# Revit family: Electronics_Visual-TVs_ViewSonic_The-ViewSonicR-CDE7500-Series-Large-Form
name_source: partatom
category: Electrical Equipment
revit_build: Autodesk Revit 2015 (Build: 20140606_1530(x64)
units: mm (PartAtom-declared; Revit-internal decimal feet)

## types (1)
- CDE7500
    Assembly Code = D50
    BIMobject category = Visual - TVs
    BIMobject category code = electronics-visual-tvs
    BIMobject main category = Electronics
    BIMobject main category code = electronics
    BOSUseNativeGeometries = 1
    Brand url = https://www.viewsonic.com
    Covering Color = Plastic - Viewsonic - Black
    Description = The ViewSonic® CDE7500 is a 75’’ (75” viewable) 4K Ultra HD commercial display with 3840 x 2160 resolution, 450-nit high brightness, wide viewing angles, and dual 20W speakers, providing high-impact messaging in hotels, restaurants, and other businesses. In addition to HDMI and VGA inputs to connect with various high definition devices, this display utilizes an integrated quad-core processor and 16GB of internal memory, allowing customers to playback multimedia content via USB without the need for a PC. To make life even easier, the bundled vController software offers easy maintenance and intuitive interfaces for remote management via a PC server or laptop, and its flicker-free and blue light filter technologies help provide a comfortable viewing environment.
    Design country = Taiwan
    Edition number = 1
    Keynote = V90
    Manufacturer = ViewSonic
    Manufacturer country = Taiwan
    Manufacturer name = ViewSonic
    Model = viewsonic_cde7500
    Product Guid = b6c1e6bf-e6e5-4bdd-9af3-737d81d68077
    Product SKU = viewsonic_cde7500
    Product data url = https://bimobject.com
    Product family = Electronics
    Product group = Large Format Displays
    Product name = The ViewSonic® CDE7500 Series Large Format Displays
    Product url = https://www.viewsonic.com
    QR code = http://bimobject.com
    URL = www.viewsonic.com
    Youtube clip = https://www.youtube.com

## geometry (parser evidence)
native form markers: Sweep x3
no freeform markers — native parametric forms only
